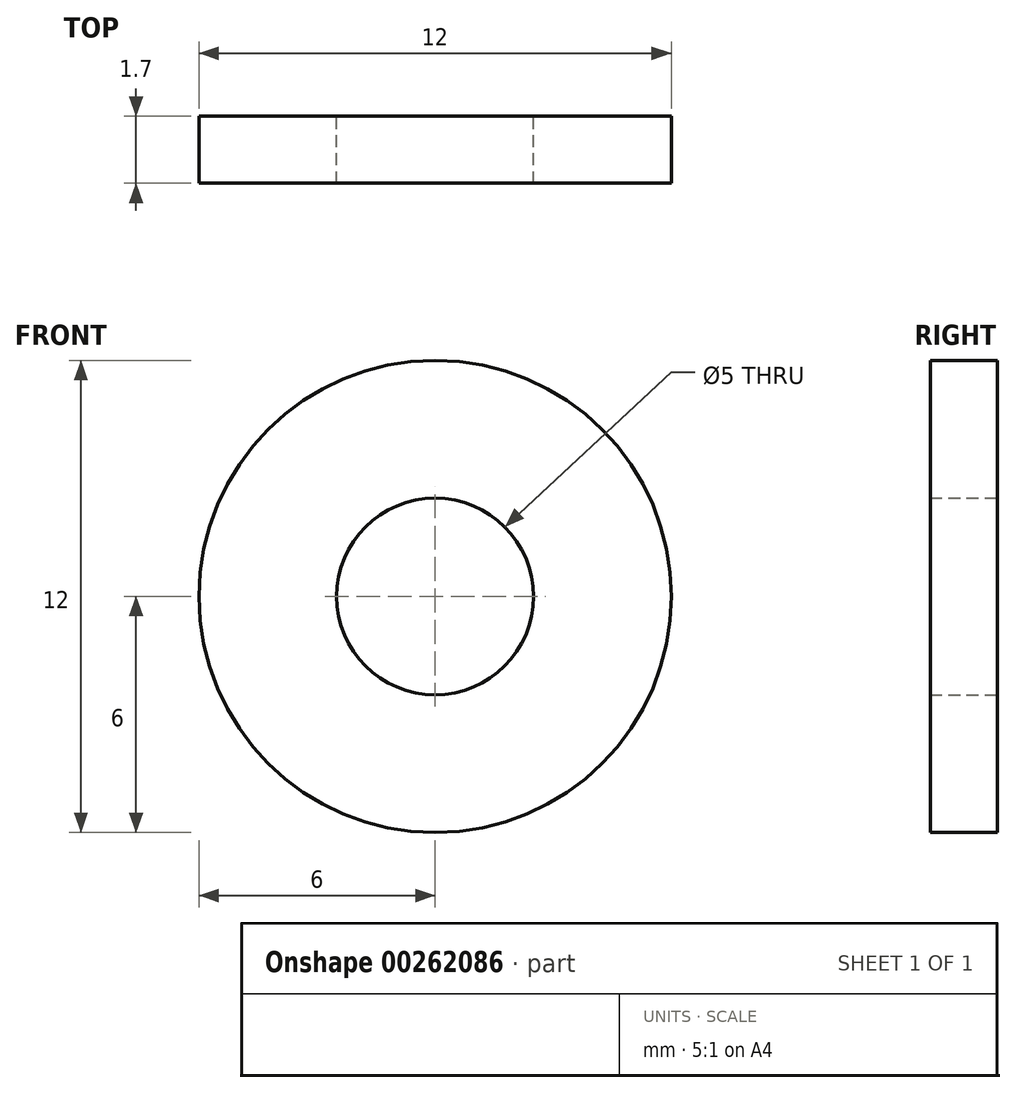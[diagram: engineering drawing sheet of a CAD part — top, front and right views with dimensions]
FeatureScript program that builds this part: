
annotation { "Feature Type Name" : "Feature", "Feature Type Description" : "" }
export const myFeature = defineFeature(function(context is Context, id is Id, definition is map)
    precondition{}
    {
        {
            assignVariable(context, id + "F0", {"name" : "Depth", "anyValue" : 1.7});
        }
        {
            assignVariable(context, id + "F1", {"name" : "Inner_Diameter", "anyValue" : 5});
        }
        {
            assignVariable(context, id + "F2", {"name" : "Di", "anyValue" : getVariable(context, 'Inner_Diameter')});
        }
        {
            var Q0;
            Q0=qCreatedBy(makeId("Front.planeOp"),FACE);
            var sketch = newSketch(context, id + "F3", { "sketchPlane" : qUnion([Q0])});
            skCircle(sketch, "E0", {"center": v(0, 0) * mm, "radius": 6 * mm});
            skSolve(sketch);
        }
        {
            var Q0;
            Q0=makeQuery(id+"F3.imprint","IMPRINT",FACE,{"disambiguationData":[TD([[makeQuery(id+"F3.imprint","IMPRINT",EDGE,{"derivedFrom":sQuery(id+"F3.wireOp",EDGE,"E0")}),1.0]])]});
            var Q1;
            Q1=sQuery(id+"F3.wireOp",EDGE,"E0");
            extrude(context, id + "F4", {"entities" : qUnion([Q0]), "surfaceEntities" : qUnion([Q1]), "depth" : (getVariable(context, 'Depth')) * mm});
        }
        {
            var Q0;
            Q0=makeQuery(id+"F4.opExtrude","CAP_FACE",FACE,{"disambiguationData":[OSD([sQuery(id+"F3.wireOp",EDGE,"E0")])],"isStart":false});
            var sketch = newSketch(context, id + "F5", { "sketchPlane" : qUnion([Q0])});
            skPoint(sketch, "E1", {"position": v(0, 0) * mm});
            skSolve(sketch);
        }
        {
            var Q0;
            Q0=sQuery(id+"F5.wireOp",VERTEX,"E1");
            var Q1;
            Q1=makeQuery(id+"F4.opExtrude","SWEPT_BODY",BODY,{"disambiguationData":[OSD([sQuery(id+"F3.wireOp",EDGE,"E0")])]});
            hole(context, id + "F6", {"style" : HoleStyle.SIMPLE, "endStyle" : HoleEndStyle.THROUGH, "holeDiameter" : (getVariable(context, 'Di')) * mm, "locations" : qUnion([Q0]), "scope" : qUnion([Q1]), "isTappedThrough" : true, "startStyle" : HoleStartStyle.PART});
        }
    });
